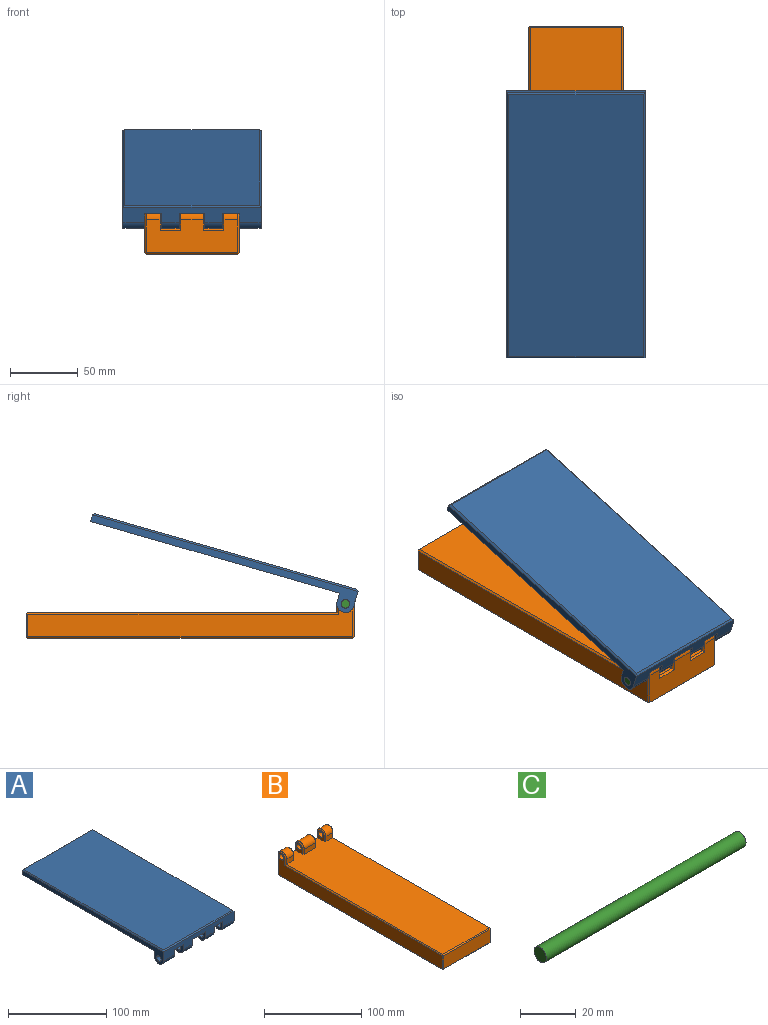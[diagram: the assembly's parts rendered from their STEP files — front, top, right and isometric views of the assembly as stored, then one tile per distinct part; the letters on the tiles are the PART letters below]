
ASSEMBLY  parts=3 mates=2
PART A: 28 faces, bbox 101.6x203.2x19.1 mm
  f0: plane 101.6x11.43mm, normal (0,-1,0), area 879mm2, adj f2,f6,f7,f9,f10,f12,f15,f17
  f1: plane 12.7x6.35mm, normal (0,1,0), area 80.6mm2, adj f2,f9,f20,f22
  f2: cylinder r=6.35mm len=12.7mm, axis (1,0,0), area 253.4mm2, adj f0,f1,f20,f22
  f3: cylinder r=3.17mm len=12.7mm, axis (1,0,0), area 253.4mm2, adj f20,f22
  f4: plane 15.88x6.35mm, normal (0,1,0), area 100.8mm2, adj f6,f9,f10,f19
  f5: plane 12.7x6.35mm, normal (0,1,0), area 80.6mm2, adj f7,f9,f18,f23
  f6: cylinder r=6.35mm len=15.88mm, axis (1,0,0), area 316.7mm2, adj f0,f4,f10,f19
  f7: cylinder r=6.35mm len=12.7mm, axis (1,0,0), area 253.4mm2, adj f0,f5,f18,f23
  f8: cylinder r=3.17mm len=15.88mm, axis (1,0,0), area 316.7mm2, adj f10,f19
  f9: plane 203.2x101.6mm, normal (0,0,-1), area 19919.3mm2, adj f0,f1,f4,f5,f10,f11,f12,f14
  f10: plane 203.2x17.78mm, normal (1,0,0), area 1144.6mm2, adj f0,f4,f6,f8,f9,f11,f25
  f11: plane 101.6x5.08mm, normal (0,1,0), area 516.1mm2, adj f9,f10,f12,f27
  f12: plane 203.2x17.78mm, normal (-1,0,0), area 1144.6mm2, adj f0,f9,f11,f14,f15,f16,f26
  f13: plane 200.66x99.06mm, normal (0,0,1), area 19877.4mm2, adj f24,f25,f26,f27
  f14: plane 15.88x6.35mm, normal (0,1,0), area 100.8mm2, adj f9,f12,f15,f17
  f15: cylinder r=6.35mm len=15.88mm, axis (1,0,0), area 316.7mm2, adj f0,f12,f14,f17
  f16: cylinder r=3.17mm len=15.88mm, axis (1,0,0), area 316.7mm2, adj f12,f17
  f17: plane 12.7x12.7mm, normal (1,0,0), area 112.3mm2, adj f0,f9,f14,f15,f16
  f18: plane 12.7x12.7mm, normal (-1,0,0), area 112.3mm2, adj f0,f5,f7,f9,f21
  f19: plane 12.7x12.7mm, normal (-1,0,0), area 112.3mm2, adj f0,f4,f6,f8,f9
  f20: plane 12.7x12.7mm, normal (1,0,0), area 112.3mm2, adj f0,f1,f2,f3,f9
  f21: cylinder r=3.17mm len=12.7mm, axis (1,0,0), area 253.4mm2, adj f18,f23
  f22: plane 12.7x12.7mm, normal (-1,0,0), area 112.3mm2, adj f0,f1,f2,f3,f9
  f23: plane 12.7x12.7mm, normal (1,0,0), area 112.3mm2, adj f0,f5,f7,f9,f21
  f24: plane 101.6x1.27mm, normal (0,-0.71,0.71), area 180.2mm2, adj f0,f13,f25,f26
  f25: plane 203.2x1.27mm, normal (0.71,0,0.71), area 362.7mm2, adj f10,f13,f24,f27
  f26: plane 203.2x1.27mm, normal (-0.71,0,0.71), area 362.7mm2, adj f12,f13,f24,f27
  f27: plane 101.6x1.27mm, normal (0,0.71,0.71), area 180.2mm2, adj f11,f13,f25,f26
PART B: 49 faces, bbox 69.9x241.3x31.8 mm
  f0: plane 67.31x24.13mm, normal (0,1,0), area 1391.9mm2, adj f1,f4,f12,f25,f26,f27,f32,f33
  f1: cylinder r=6.35mm len=12.7mm, axis (1,0,0), area 202.7mm2, adj f0,f2,f31,f45
  f2: plane 10.16x6.35mm, normal (0,-1,0), area 64.5mm2, adj f1,f10,f30,f47
  f3: cylinder r=3.17mm len=12.7mm, axis (1,0,0), area 253.4mm2, adj f9,f17
  f4: cylinder r=6.35mm len=16.51mm, axis (1,0,0), area 329.4mm2, adj f0,f5,f24,f35
  f5: plane 16.51x6.35mm, normal (0,-1,0), area 104.8mm2, adj f4,f10,f23,f36
  f6: cylinder r=3.17mm len=19.05mm, axis (1,0,0), area 380mm2, adj f16,f18
  f7: plane 238.76x29.21mm, normal (-1,0,0), area 4028.2mm2, adj f14,f19,f37,f38,f39,f40,f41
  f8: plane 67.31x16.51mm, normal (0,-1,0), area 1111.3mm2, adj f19,f20,f21,f22
  f9: plane 238.76x29.21mm, normal (1,0,0), area 4028.2mm2, adj f3,f22,f44,f45,f46,f47,f48
  f10: plane 238.76x67.31mm, normal (0,0,1), area 15595.1mm2, adj f2,f5,f13,f15,f16,f17,f18,f20
  f11: plane 238.76x67.31mm, normal (0,0,-1), area 16070.9mm2, adj f21,f41,f43,f48
  f12: cylinder r=6.35mm len=12.7mm, axis (1,0,0), area 202.7mm2, adj f0,f13,f28,f39
  f13: plane 10.16x6.35mm, normal (0,-1,0), area 64.5mm2, adj f10,f12,f29,f38
  f14: cylinder r=3.17mm len=12.7mm, axis (1,0,0), area 253.4mm2, adj f7,f15
  f15: plane 11.43x10.16mm, normal (1,0,0), area 73.4mm2, adj f10,f14,f27,f28,f29
  f16: plane 11.43x10.16mm, normal (-1,0,0), area 73.4mm2, adj f6,f10,f23,f24,f25
  f17: plane 11.43x10.16mm, normal (-1,0,0), area 73.4mm2, adj f3,f10,f30,f31,f32
  f18: plane 11.43x10.16mm, normal (1,0,0), area 73.4mm2, adj f6,f10,f34,f35,f36
  f19: plane 17.78x1.27mm, normal (-0.71,-0.71,0), area 30.8mm2, adj f7,f8,f20,f21,f37,f41
  f20: plane 68.58x1.27mm, normal (0,-0.71,0.71), area 122mm2, adj f8,f10,f19,f22,f37,f46
  f21: plane 68.58x1.27mm, normal (0,-0.71,-0.71), area 122mm2, adj f8,f11,f19,f22,f41,f48
  f22: plane 17.78x1.27mm, normal (0.71,-0.71,0), area 30.8mm2, adj f8,f9,f20,f21,f46,f48
  f23: plane 6.35x1.27mm, normal (-0.71,-0.71,0), area 11.4mm2, adj f5,f10,f16,f24
  f24: cone r=6.35mm half-angle=45deg, axis (1,0,0), area 32.2mm2, adj f4,f16,f23,f25
  f25: plane 7.62x1.27mm, normal (-0.71,0.71,0), area 12.5mm2, adj f0,f16,f24,f26
  f26: plane 15.24x1.27mm, normal (0,0.71,0.71), area 25.1mm2, adj f0,f10,f25,f27
  f27: plane 7.62x1.27mm, normal (0.71,0.71,0), area 12.5mm2, adj f0,f15,f26,f28
  f28: cone r=5.08mm half-angle=45deg, axis (-1,0,0), area 32.2mm2, adj f12,f15,f27,f29
  f29: plane 6.35x1.27mm, normal (0.71,-0.71,0), area 11.4mm2, adj f10,f13,f15,f28
  f30: plane 6.35x1.27mm, normal (-0.71,-0.71,0), area 11.4mm2, adj f2,f10,f17,f31
  f31: cone r=6.35mm half-angle=45deg, axis (1,0,0), area 32.2mm2, adj f1,f17,f30,f32
  f32: plane 7.62x1.27mm, normal (-0.71,0.71,0), area 12.5mm2, adj f0,f17,f31,f33
  f33: plane 15.24x1.27mm, normal (0,0.71,0.71), area 25.1mm2, adj f0,f10,f32,f34
  f34: plane 7.62x1.27mm, normal (0.71,0.71,0), area 12.5mm2, adj f0,f18,f33,f35
  f35: cone r=5.08mm half-angle=45deg, axis (-1,0,0), area 32.2mm2, adj f4,f18,f34,f36
  f36: plane 6.35x1.27mm, normal (0.71,-0.71,0), area 11.4mm2, adj f5,f10,f18,f35
  f37: plane 229.24x1.27mm, normal (-0.71,0,0.71), area 410mm2, adj f7,f10,f19,f20,f38
  f38: plane 7.62x1.27mm, normal (-0.71,-0.71,0), area 12.5mm2, adj f7,f13,f37,f39
  f39: cone r=6.35mm half-angle=45deg, axis (1,0,0), area 32.2mm2, adj f7,f12,f38,f40
  f40: plane 24.13x1.27mm, normal (-0.71,0.71,0), area 43.3mm2, adj f0,f7,f39,f42
  f41: plane 239.4x1.27mm, normal (-0.71,0,-0.71), area 429.4mm2, adj f7,f11,f19,f21,f42
  f42: plane 1.27x1.27mm, normal (-0.58,0.58,-0.58), area 1.4mm2, adj f40,f41,f43
  f43: plane 67.95x1.27mm, normal (0,0.71,-0.71), area 121.5mm2, adj f0,f11,f42,f44,f48
  f44: plane 24.77x1.27mm, normal (0.71,0.71,0), area 43.9mm2, adj f0,f9,f43,f45,f48
  f45: cone r=5.08mm half-angle=45deg, axis (-1,0,0), area 32.2mm2, adj f1,f9,f44,f47
  f46: plane 229.24x1.27mm, normal (0.71,0,0.71), area 410mm2, adj f9,f10,f20,f22,f47
  f47: plane 7.62x1.27mm, normal (0.71,-0.71,0), area 12.5mm2, adj f2,f9,f45,f46
  f48: plane 240.03x1.27mm, normal (0.71,0,-0.71), area 430mm2, adj f9,f11,f21,f22,f43,f44
PART C: 3 faces, bbox 101.6x6.4x6.4 mm
  f0: cylinder r=3.17mm len=101.6mm, axis (-1,0,0), area 2026.8mm2, adj f1,f2
  f1: plane 6.35x6.35mm, normal (1,0,0), area 31.7mm2, adj f0
  f2: plane 6.35x6.35mm, normal (-1,0,0), area 31.7mm2, adj f0
PLACE A rot(axis=(1,0,0),16.1deg) t=(5.57,-18.38,61.88)mm
PLACE B rot(axis=(0,0,1),180deg) t=(5.57,6.15,4)mm fixed
PLACE C t=(-45.23,-108.15,29.4)mm
MATE revolute C.f0 <-> A.f2  axis (1,0,0) through (56.37,-108.15,29.4)mm
MATE cylindrical C.f0 <-> B.f1  axis (1,0,0) through (56.37,-108.15,29.4)mm
